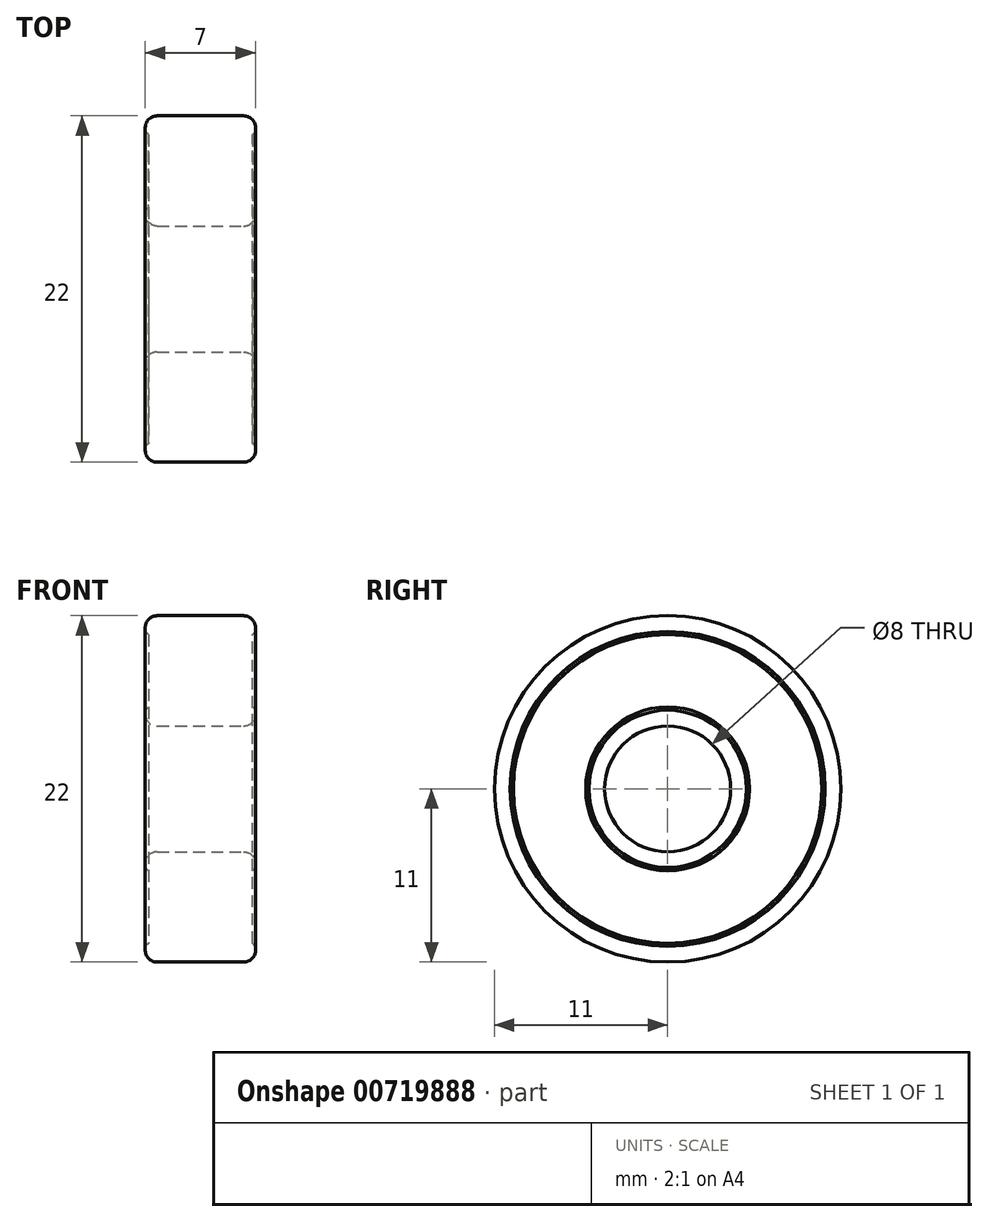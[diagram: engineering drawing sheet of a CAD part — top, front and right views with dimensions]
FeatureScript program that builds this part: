
annotation { "Feature Type Name" : "Feature", "Feature Type Description" : "" }
export const myFeature = defineFeature(function(context is Context, id is Id, definition is map)
    precondition{}
    {
        {
            var Q0;
            Q0=qCreatedBy(makeId("Front.planeOp"),FACE);
            var sketch = newSketch(context, id + "F0", { "sketchPlane" : qUnion([Q0])});
            skLineSegment(sketch, "E0.bottom", {"start": v(-3.5, 11) * mm, "end": v(3.5, 11) * mm});
            skLineSegment(sketch, "E0.top", {"start": v(-3.5, 4) * mm, "end": v(3.5, 4) * mm});
            skLineSegment(sketch, "E0.left", {"start": v(-3.5, 11) * mm, "end": v(-3.5, 4) * mm});
            skLineSegment(sketch, "E0.right", {"start": v(3.5, 11) * mm, "end": v(3.5, 4) * mm});
            skPoint(sketch, "E1", {"position": v(0, 11) * mm});
            skLineSegment(sketch, "E2", {"start": v(5.31, 0) * mm, "end": v(-6.65, 0) * mm, "construction": true});
            skSolve(sketch);
        }
        {
            var Q0;
            Q0=qSketchRegion(id+"F0",true);
            var Q1;
            Q1=sQuery(id+"F0.wireOp",EDGE,"E2");
            revolve(context, id + "F1", {"entities" : qUnion([Q0]), "axis" : qUnion([Q1]), "revolveType" : RevolveType.FULL});
        }
        {
            var Q0;
            Q0=makeQuery(id+"F1.opRevolve","SWEPT_EDGE",EDGE,{"disambiguationData":[OSD([sQuery(id+"F0.wireOp",EDGE,"E0.bottom"),sQuery(id+"F0.wireOp",EDGE,"E0.left")])]});
            var Q1;
            Q1=makeQuery(id+"F1.opRevolve","SWEPT_EDGE",EDGE,{"disambiguationData":[OSD([sQuery(id+"F0.wireOp",EDGE,"E0.top"),sQuery(id+"F0.wireOp",EDGE,"E0.left")])]});
            var Q2;
            Q2=makeQuery(id+"F1.opRevolve","SWEPT_EDGE",EDGE,{"disambiguationData":[OSD([sQuery(id+"F0.wireOp",EDGE,"E0.bottom"),sQuery(id+"F0.wireOp",EDGE,"E0.right")])]});
            var Q3;
            Q3=makeQuery(id+"F1.opRevolve","SWEPT_EDGE",EDGE,{"disambiguationData":[OSD([sQuery(id+"F0.wireOp",EDGE,"E0.top"),sQuery(id+"F0.wireOp",EDGE,"E0.right")])]});
            fillet(context, id + "F2", {"entities" : qUnion([Q0, Q1, Q2, Q3]), "radius" : 0.75 * mm, "tangentPropagation" : true, "allowEdgeOverflow" : false});
        }
        {
            var Q0;
            Q0=qCreatedBy(makeId("Top.planeOp"),FACE);
            var sketch = newSketch(context, id + "F3", { "sketchPlane" : qUnion([Q0])});
            skLineSegment(sketch, "E3", {"start": v(-5.02, 0) * mm, "end": v(5.29, 0) * mm});
            skLineSegment(sketch, "E4", {"start": v(-3.5, -10) * mm, "end": v(-3.3, -10) * mm});
            skLineSegment(sketch, "E5", {"start": v(-3.3, -10) * mm, "end": v(-3.3, -5) * mm});
            skLineSegment(sketch, "E6", {"start": v(-3.3, -5) * mm, "end": v(-3.5, -5) * mm});
            skLineSegment(sketch, "E7", {"start": v(-3.5, -5) * mm, "end": v(-3.5, -10) * mm});
            skLineSegment(sketch, "E8", {"start": v(3.3, -10) * mm, "end": v(3.5, -10) * mm});
            skPoint(sketch, "E8.startSnap0", {"position": v(-3.4, -10) * mm});
            skLineSegment(sketch, "E9", {"start": v(3.5, -10) * mm, "end": v(3.5, -5) * mm});
            skLineSegment(sketch, "E10", {"start": v(3.5, -5) * mm, "end": v(3.3, -5) * mm});
            skLineSegment(sketch, "E11", {"start": v(3.3, -5) * mm, "end": v(3.3, -10) * mm});
            skSolve(sketch);
        }
        {
            var Q0;
            Q0 = qSketchRegion(id + "F3", true);
            var Q1;
            Q1=sQuery(id+"F3.wireOp",EDGE,"E3");
            revolve(context, id + "F4", {"operationType" : NewBodyOperationType.REMOVE, "surfaceOperationType" : NewSurfaceOperationType.NEW, "entities" : qUnion([Q0]), "axis" : qUnion([Q1]), "revolveType" : RevolveType.FULL, "oppositeDirection" : true});
        }
        {
            var Q0;
            Q0=makeQuery(id+"F4.boolean.opBoolean","COPY",EDGE,{"derivedFrom":makeQuery(id+"F4.opRevolve","SWEPT_EDGE",EDGE,{"disambiguationData":[OSD([sQuery(id+"F3.wireOp",EDGE,"E4"),sQuery(id+"F3.wireOp",EDGE,"E5")])]})});
            var Q1;
            Q1=makeQuery(id+"F4.boolean.opBoolean","COPY",EDGE,{"derivedFrom":makeQuery(id+"F4.opRevolve","SWEPT_EDGE",EDGE,{"disambiguationData":[OSD([sQuery(id+"F3.wireOp",EDGE,"E5"),sQuery(id+"F3.wireOp",EDGE,"E6")])]})});
            var Q2;
            Q2=makeQuery(id+"F4.boolean.opBoolean","COPY",EDGE,{"derivedFrom":makeQuery(id+"F4.opRevolve","SWEPT_EDGE",EDGE,{"disambiguationData":[OSD([sQuery(id+"F3.wireOp",EDGE,"E8"),sQuery(id+"F3.wireOp",EDGE,"E11")])]})});
            var Q3;
            Q3=makeQuery(id+"F4.boolean.opBoolean","COPY",EDGE,{"derivedFrom":makeQuery(id+"F4.opRevolve","SWEPT_EDGE",EDGE,{"disambiguationData":[OSD([sQuery(id+"F3.wireOp",EDGE,"E10"),sQuery(id+"F3.wireOp",EDGE,"E11")])]})});
            chamfer(context, id + "F5", {"entities" : qUnion([Q0, Q1, Q2, Q3]), "width" : .2 * mm, "tangentPropagation" : true});
        }
    });
